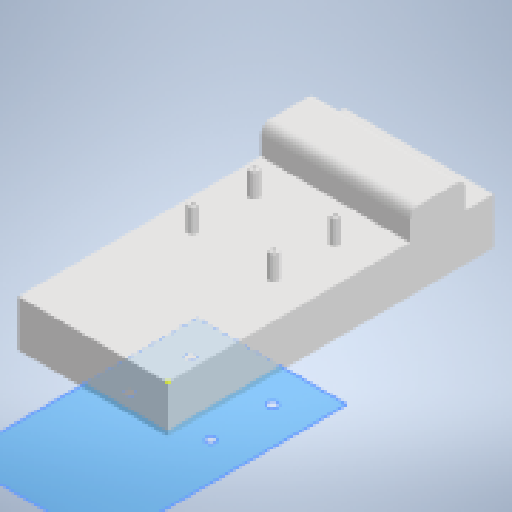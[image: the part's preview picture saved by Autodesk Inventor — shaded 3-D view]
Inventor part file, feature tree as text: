
AUTODESK INVENTOR PART (.ipt)
format: ipt  version: 2024.2 (Build 282272000, 272)  size: 278,528 bytes
history: native  units: mm
features: sketch x5, extrude x4, fillet x1
ambient origin geometry x8: Origin, YZ Plane, XZ Plane, XY Plane, X Axis, Y Axis, Z Axis, Center Point
bodies: Solid1 (feature_tree)
feature tree (10):
  extrude  "Extrusion1"  Depth=175.0mm
  sketch  "Sketch2"  dims[d2=25.0mm d3=0.0mm d4=15.0mm d5=15.0mm]
  extrude  "Extrusion2"  Depth=15.0mm
  fillet  "Fillet1"  Radius=15.0mm
  extrude  "Extrusion3"  Depth=80.0mm TaperAngle=0.0deg
  extrude  "Extrusion4"  Depth=5.0mm
  sketch  "Sketch1"  dims[d0=80.0mm d1=175.0mm]
  sketch  "Sketch3"  dims[d6=30.0mm d7=80.0mm d8=0.0mm]
  sketch  "Sketch4"  dims[d9=5.0mm d10=5.0mm]
  sketch  "Sketch5"  dims[d11=5.0mm d12=5.0mm d13=5.0mm d14=20.0mm d15=20.0mm d16=43.5mm d17=43.5mm d18=20.0mm d19=20.0mm d20=33.0mm d21=33.0mm d22=13.0mm d23=0.0mm d24=2.0mm d25=2.0mm d26=2.0mm d27=2.0mm d28=13.0mm d29=0.0mm]
